# Revit family: Sigma_Compact_DN025_LF_RFA_2019
name_source: partatom
category: Pipe Accessories
units: mm (PartAtom-declared; Revit-internal decimal feet)

## family parameters
Always vertical = Yes
Cut with Voids When Loaded = No
Part Type = Valve - Breaks Into
Round Connector Dimension = Use Diameter
Shared = No
Work Plane-Based = No

## types (3) — shared parameters
C0D0 = Yes
C0D1 = No
CAT0 = Yes
DL2 = 66 mm
DR0 = Yes
DR1 = No
Description = Automatický vyvažovací ventil
L2D = 65 mm
L2D_Min = 30 mm  [stored 0.0984252 ft]
L3 = 11 mm  [stored 0.0360892 ft]
LL = 6 mm  [stored 0.019685 ft]
LL3 = 41 mm  [stored 0.134514 ft]
LL__ve = -6 mm  [stored -0.019685 ft]
MC Pressure Drop Maximum Value = 0.0 Pa
MC Pressure Drop Minimum Value = 0.0 Pa
MC Use Limits From Balancing Method = No
Manufacturer = Hydronic Systems Prague s.r.o.
QmdConnectorList = 301;D;302;D
R1 = 19 mm  [stored 0.062336 ft]
R3 = 10 mm  [stored 0.0328084 ft]
R4 = 15 mm  [stored 0.0492126 ft]
Type Comments = závitový; vnitřní závit; PN25; max dp=400kPa; -10~+120°C; max uzavírací tlak 1MPa
URL = www.hydronic.cz
W2D = 15 mm  [stored 0.0492126 ft]
XR1 = 13 mm  [stored 0.0426509 ft]
XR2 = 25 mm  [stored 0.082021 ft]
Z3 = 9 mm  [stored 0.0295276 ft]
magiPartTypeId = 304
magiProductFamilyId = 899bca4e67ce4698b7af5040674aaa
zero-valued in all types: MC Throttling Maximum Value, MC Throttling Minimum Value

## per-type parameters (varying)
| type | CenSd_R2_6 | D | LL2 | LLL | LLT | LLT__ve | LM | LP | M2 | M3 | M4 | M5 | MC Product Code | NL | NL__ve | R2 | Z2 | Z4 | Z5 | Z6 | magiProductId |
| Sigma Compact DN 15 LF s měřením | 12 mm  [stored 0.0393701 ft] | 15 mm | 32 mm  [stored 0.104987 ft] | 11 mm  [stored 0.0360892 ft] | 15 mm  [stored 0.0492126 ft] | -15 mm  [stored -0.0492126 ft] | 45 mm  [stored 0.147638 ft] | 38 mm | 23 mm | 25 mm  [stored 0.082021 ft] | 31 mm | 33 mm | 53-2200 DN15 FF s měřením; (40-900 l/h); kvs=2,6 | 15 mm  [stored 0.0492126 ft] | -15 mm  [stored -0.0492126 ft] | 14 mm  [stored 0.0459318 ft] | 44 mm  [stored 0.144357 ft] | 52 mm | 61 mm | 26 mm  [stored 0.0853018 ft] | 4a904ca02dcd4d4b8bc93e9b7121ab |
| Sigma Compact DN 20 LF s měřením | 12 mm  [stored 0.0393701 ft] | 20 mm | 32 mm  [stored 0.104987 ft] | 11 mm  [stored 0.0360892 ft] | 15 mm  [stored 0.0492126 ft] | -15 mm  [stored -0.0492126 ft] | 47 mm | 40 mm | 24 mm | 26 mm  [stored 0.0853018 ft] | 32 mm  [stored 0.104987 ft] | 34 mm  [stored 0.111549 ft] | 53-2202 DN20 FF s měřením; (86-1550 l/h); kvs=4,0 | 16 mm | -16 mm  [stored -0.0524934 ft] | 14 mm  [stored 0.0459318 ft] | 44 mm  [stored 0.144357 ft] | 52 mm | 61 mm | 26 mm  [stored 0.0853018 ft] | 530dd69e715c4b5ea08f3ea7c41338 |
| Sigma Compact DN 25 LF s měřením | 16 mm | 25 mm | 34 mm  [stored 0.111549 ft] | 9 mm  [stored 0.0295276 ft] | 16 mm | -16 mm  [stored -0.0524934 ft] | 50 mm  [stored 0.164042 ft] | 42 mm | 25 mm  [stored 0.082021 ft] | 27 mm | 33 mm | 35 mm | 53-2208 DN25 FF s měřením; (95-2000 l/h); kvs=3,9 | 17 mm | -17 mm  [stored -0.0557743 ft] | 18 mm  [stored 0.0590551 ft] | 45 mm  [stored 0.147638 ft] | 54 mm  [stored 0.177165 ft] | 63 mm  [stored 0.206693 ft] | 27 mm | bcbd50229c6f49259ed1f55c66b3ed |

note: [stored X ft] marks values corroborated as IEEE doubles in the binary element streams (Revit-internal decimal feet)

## geometry (parser evidence)
native form markers: Sweep x1
no freeform markers — native parametric forms only
